# Revit family: UL924BRUNV
name_source: partatom
category: Communication Devices
revit_build: Autodesk Revit 2014 (Build: 20130308_1515(x64)
units: mm (PartAtom-declared; Revit-internal decimal feet)

## types (1)
- UL924BRUNV
    Assembly Code = D5090
    Black = Paint - Hubbell - Carbon Black
    Default Elevation = 48 "
    Description = Hubbell Control Solutions enclosed 20 amp emergency load control relay is specifically designed for applications that require the control of emergency light fixtures along with the general lighting in a space. This type of emergency lighting is often referred to as “always on”. The UL924BRUNV connects to the line side of the control device to sense the presence of “normal” power. It also connects to the load side of the control device to provide an ON/OFF signal for control of the emergency lights along with the general lighting. When normal power is lost, control is suspended and the normally closed relay provides emergency power to the emergency fixtures.
    Features = 20 Amp, normally closed relay
120 or 277 volt operation
UL924 Listed
No minimum load requirement
Five-year warranty
    Gray = Paint - Hubbell - Gray Smooth
    Height = 4.5 "
    Manufacturer = Hubbell Control Solutions
    Model = UL924BRUNV
    Product Documentation Link = https://hubbellcdn.com
    Product Page URL = https://www.hubbell.com
    Type Comments = Bypass Relays
    URL = https://www.hubbell.com
    Warranty = 5-Years Warranty
    Width = 2.75 "

## geometry (parser evidence)
native form markers: Sweep x1
no freeform markers — native parametric forms only
